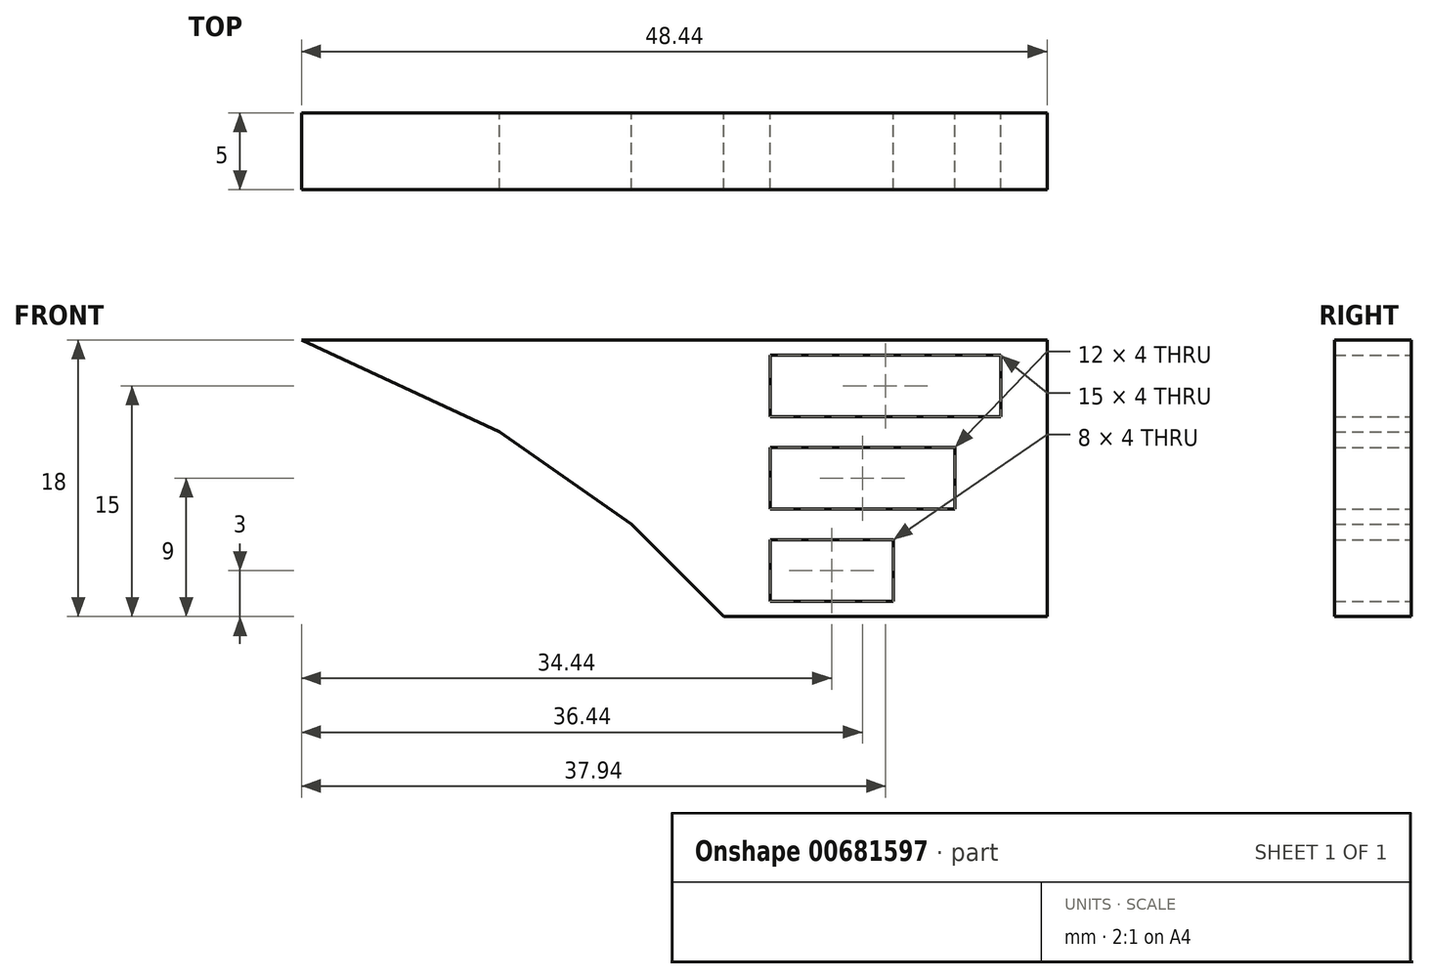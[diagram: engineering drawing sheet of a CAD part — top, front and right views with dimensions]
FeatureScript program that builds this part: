
annotation { "Feature Type Name" : "Feature", "Feature Type Description" : "" }
export const myFeature = defineFeature(function(context is Context, id is Id, definition is map)
    precondition{}
    {
        {
            var Q0;
            Q0=qCreatedBy(makeId("Front.planeOp"),FACE);
            var sketch = newSketch(context, id + "F0", { "sketchPlane" : qUnion([Q0])});
            skLineSegment(sketch, "E0", {"start": v(0, 0) * mm, "end": v(-3, 0) * mm});
            skLineSegment(sketch, "E1", {"start": v(-3, 0) * mm, "end": v(-9, 6) * mm});
            skLineSegment(sketch, "E2", {"start": v(-9, 6) * mm, "end": v(0, 6) * mm, "construction": true});
            skLineSegment(sketch, "E3", {"start": v(0, 6) * mm, "end": v(0, 0) * mm, "construction": true});
            skLineSegment(sketch, "E4", {"start": v(-9, 6) * mm, "end": v(-17.57, 12) * mm});
            skLineSegment(sketch, "E5", {"start": v(-17.57, 12) * mm, "end": v(0, 12) * mm, "construction": true});
            skLineSegment(sketch, "E6", {"start": v(0, 12) * mm, "end": v(0, 6) * mm, "construction": true});
            skLineSegment(sketch, "E7", {"start": v(-17.57, 12) * mm, "end": v(-30.44, 18) * mm});
            skLineSegment(sketch, "E8", {"start": v(-30.44, 18) * mm, "end": v(0, 18) * mm});
            skLineSegment(sketch, "E9", {"start": v(0, 18) * mm, "end": v(0, 12) * mm, "construction": true});
            skLineSegment(sketch, "E10.top", {"start": v(0, 0) * mm, "end": v(18, 0) * mm});
            skLineSegment(sketch, "E11.left", {"start": v(0, 6) * mm, "end": v(0, 12) * mm, "construction": true});
            skLineSegment(sketch, "E12.top", {"start": v(0, 18) * mm, "end": v(18, 18) * mm});
            skLineSegment(sketch, "E12.left", {"start": v(0, 12) * mm, "end": v(0, 18) * mm, "construction": true});
            skLineSegment(sketch, "E12.right", {"start": v(18, 0) * mm, "end": v(18, 18) * mm});
            skLineSegment(sketch, "E13.bottom", {"start": v(0, 1) * mm, "end": v(8, 1) * mm});
            skLineSegment(sketch, "E13.top", {"start": v(0, 5) * mm, "end": v(8, 5) * mm});
            skLineSegment(sketch, "E13.left", {"start": v(0, 1) * mm, "end": v(0, 5) * mm});
            skLineSegment(sketch, "E13.right", {"start": v(8, 1) * mm, "end": v(8, 5) * mm});
            skLineSegment(sketch, "E14.bottom", {"start": v(0, 7) * mm, "end": v(12, 7) * mm});
            skLineSegment(sketch, "E14.top", {"start": v(0, 11) * mm, "end": v(12, 11) * mm});
            skLineSegment(sketch, "E14.left", {"start": v(0, 7) * mm, "end": v(0, 11) * mm, "construction": true});
            skLineSegment(sketch, "E14.right", {"start": v(12, 7) * mm, "end": v(12, 11) * mm});
            skLineSegment(sketch, "E15.bottom", {"start": v(0, 13) * mm, "end": v(15, 13) * mm});
            skLineSegment(sketch, "E15.top", {"start": v(0, 17) * mm, "end": v(15, 17) * mm});
            skLineSegment(sketch, "E15.left", {"start": v(0, 13) * mm, "end": v(0, 17) * mm});
            skLineSegment(sketch, "E15.right", {"start": v(15, 13) * mm, "end": v(15, 17) * mm});
            skLineSegment(sketch, "E16", {"start": v(0, 11) * mm, "end": v(0, 7) * mm});
            skSolve(sketch);
        }
        {
            var Q0;
            Q0=makeQuery(id+"F0.imprint","IMPRINT",FACE,{"disambiguationData":[TD([[makeQuery(id+"F0.imprint","IMPRINT",EDGE,{"derivedFrom":sQuery(id+"F0.wireOp",EDGE,"E0")}),-1.0]])]});
            extrude(context, id + "F1", {"entities" : qUnion([Q0]), "depth" : 5 * mm, "offsetDistance" : 25 * mm});
        }
    });
